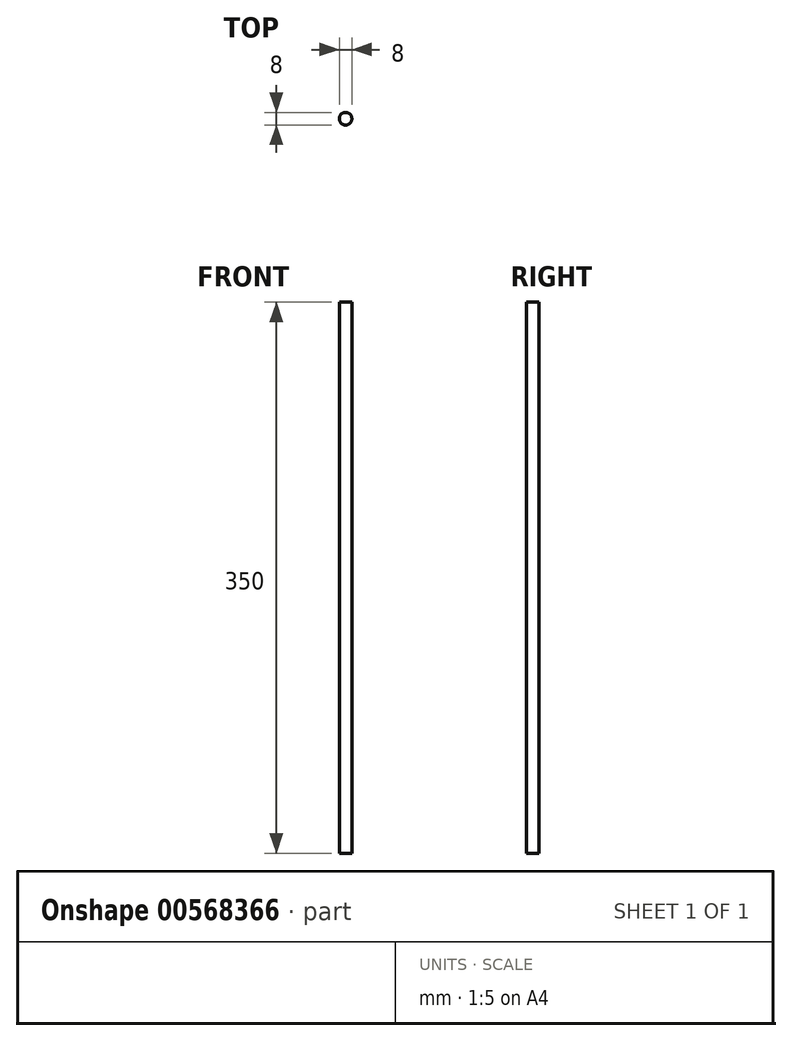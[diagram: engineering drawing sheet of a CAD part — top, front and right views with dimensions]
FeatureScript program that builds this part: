
annotation { "Feature Type Name" : "Feature", "Feature Type Description" : "" }
export const myFeature = defineFeature(function(context is Context, id is Id, definition is map)
    precondition{}
    {
        {
            var Q0;
            Q0=qCreatedBy(makeId("Top.planeOp"),FACE);
            var sketch = newSketch(context, id + "F0", { "sketchPlane" : qUnion([Q0])});
            skCircle(sketch, "E0", {"center": v(0, 0) * mm, "radius": 4 * mm});
            skPoint(sketch, "E1.middle", {"position": v(0, 4) * mm});
            skCircle(sketch, "E2", {"center": v(0, 0) * mm, "radius": 11 * mm});
            skLineSegment(sketch, "E3.bottom", {"start": v(5.5, -5.5) * mm, "end": v(-5.5, -5.5) * mm, "construction": true});
            skLineSegment(sketch, "E3.top", {"start": v(5.5, 5.5) * mm, "end": v(-5.5, 5.5) * mm, "construction": true});
            skLineSegment(sketch, "E3.left", {"start": v(5.5, -5.5) * mm, "end": v(5.5, 5.5) * mm, "construction": true});
            skLineSegment(sketch, "E3.right", {"start": v(-5.5, -5.5) * mm, "end": v(-5.5, 5.5) * mm, "construction": true});
            skCircle(sketch, "E4", {"center": v(-5.5, 5.5) * mm, "radius": 1.75 * mm});
            skCircle(sketch, "E5", {"center": v(5.5, 5.5) * mm, "radius": 1.75 * mm});
            skCircle(sketch, "E6", {"center": v(5.5, -5.5) * mm, "radius": 1.75 * mm});
            skCircle(sketch, "E7", {"center": v(-5.5, -5.5) * mm, "radius": 1.75 * mm});
            skCircle(sketch, "E8", {"center": v(0, 0) * mm, "radius": 5 * mm});
            skSolve(sketch);
        }
        {
            var Q0;
            Q0=makeQuery(id+"F0.imprint","IMPRINT",FACE,{"disambiguationData":[TD([[makeQuery(id+"F0.imprint","IMPRINT",EDGE,{"derivedFrom":sQuery(id+"F0.wireOp",EDGE,"E0")}),1.0]])]});
            extrude(context, id + "F1", {"entities" : qUnion([Q0]), "depth" : 350 * mm, "offsetDistance" : 25 * mm});
        }
    });
